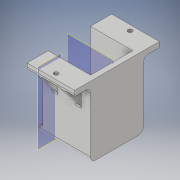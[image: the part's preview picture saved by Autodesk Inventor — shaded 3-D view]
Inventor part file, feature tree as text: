
AUTODESK INVENTOR PART (.ipt)
format: ipt  version: 2019.4 (Build 234330000, 330)  size: 207,872 bytes
history: native  units: mm
features: fillet x6, extrude x5, sketch x5, plane x2, pattern_linear x1, mirror x1
ambient origin geometry x8: Origin, YZ Plane, XZ Plane, XY Plane, X Axis, Y Axis, Z Axis, Center Point
bodies: Solid1 (feature_tree)
feature tree (20):
  extrude  "Extrusion1"  Depth=40.0mm
  extrude  "Extrusion2"  Depth=67.0mm TaperAngle=0.0deg
  plane  "Work Plane1"
  extrude  "Extrusion3"  Depth=50.0mm
  plane  "Work Plane2"
  extrude  "Extrusion4"  Depth=20.0mm
  pattern_linear  "Rectangular Pattern1"  Spacing1=5.0mm  [1 undecoded]
  fillet  "Fillet1"  Radius=15.0mm
  fillet  "Fillet2"  [1 undecoded]
  mirror  "Mirror1"
  fillet  "Fillet3"  Radius=25.0mm
  fillet  "Fillet4"  Radius=15.0mm
  fillet  "Fillet5"  Radius=5.0mm
  fillet  "Fillet6"  Radius=20.0mm
  extrude  "Extrusion6"  Depth=5.0mm
  sketch  "Sketch1"  dims[d0=40.0mm d1=40.0mm]
  sketch  "Sketch2"  dims[d2=5.0mm d3=67.0mm d4=0.0mm]
  sketch  "Sketch3"  dims[d5=50.0mm d6=50.0mm]
  sketch  "Sketch4"  dims[d7=5.0mm d8=0.0mm d9=20.0mm]
  sketch  "Sketch6"  dims[d10=45.0mm d11=5.0mm d12=15.0mm d13=0.0mm d14=-11.25mm d15=25.0mm d17=15.0mm d18=5.0mm d19=0.0mm d20=20.0mm d22=22.5mm d23=5.0mm d24=5.0mm d25=5.0mm d26=5.0mm d27=5.0mm d28=5.0mm d35=5.0mm d36=5.0mm d37=4.0mm d38=4.0mm d39=5.0mm d40=0.0mm]
note: 2 required parameter values undecoded (feature->parameter linkage not recoverable at this tier; creation-order binding heuristic only, values carry confidence <= 0.55)
